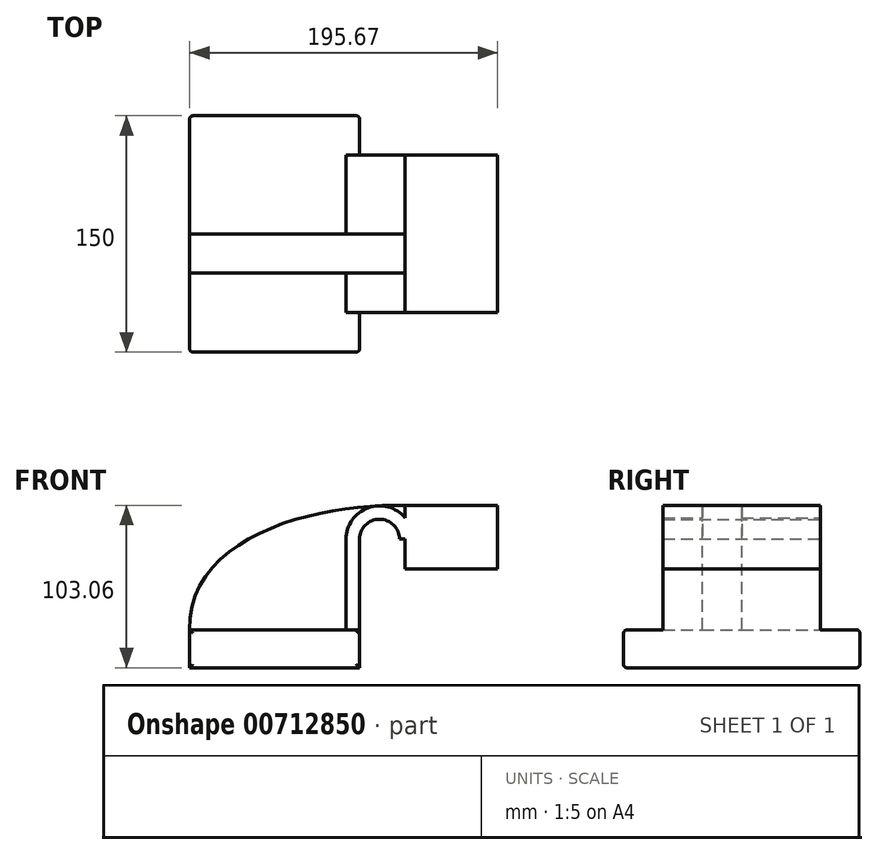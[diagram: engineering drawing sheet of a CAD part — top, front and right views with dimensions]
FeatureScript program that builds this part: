
annotation { "Feature Type Name" : "Feature", "Feature Type Description" : "" }
export const myFeature = defineFeature(function(context is Context, id is Id, definition is map)
    precondition{}
    {
        {
            var Q0;
            Q0=qCreatedBy(makeId("Front.planeOp"),FACE);
            var sketch = newSketch(context, id + "F0", { "sketchPlane" : qUnion([Q0])});
            skLineSegment(sketch, "E0.bottom", {"start": v(-53.96, 12) * mm, "end": v(53.96, 12) * mm});
            skLineSegment(sketch, "E0.top", {"start": v(-53.96, -12) * mm, "end": v(53.96, -12) * mm});
            skLineSegment(sketch, "E0.left", {"start": v(-53.96, 12) * mm, "end": v(-53.96, -12) * mm});
            skLineSegment(sketch, "E0.right", {"start": v(53.96, 12) * mm, "end": v(53.96, -12) * mm});
            skPoint(sketch, "E0.middle", {"position": v(0, 0) * mm});
            skLineSegment(sketch, "E1.bottom", {"start": v(82.9, 50.87) * mm, "end": v(141.7, 50.87) * mm});
            skLineSegment(sketch, "E1.top", {"start": v(82.9, 90.9) * mm, "end": v(141.7, 90.9) * mm});
            skLineSegment(sketch, "E1.left", {"start": v(82.9, 50.87) * mm, "end": v(82.9, 90.9) * mm});
            skLineSegment(sketch, "E1.right", {"start": v(141.7, 50.87) * mm, "end": v(141.7, 90.9) * mm});
            skPoint(sketch, "E1.middle", {"position": v(112.3, 70.89) * mm});
            skLineSegment(sketch, "E2", {"start": v(53.96, 12) * mm, "end": v(53.96, 69.64) * mm});
            skArc(sketch, "E3", {"start": v(53.96, 69.64) * mm, "mid": v(66.63, 82.31) * mm, "end": v(79.3, 69.64) * mm});
            skLineSegment(sketch, "E4", {"start": v(79.3, 69.64) * mm, "end": v(104.51, 69.64) * mm});
            skLineSegment(sketch, "E5.0", {"start": v(86.04, 78.16) * mm, "end": v(104.51, 78.16) * mm});
            skArc(sketch, "E5.1", {"start": v(45.43, 69.64) * mm, "mid": v(62.28, 90.38) * mm, "end": v(86.04, 78.16) * mm});
            skLineSegment(sketch, "E5.2", {"start": v(45.43, 12) * mm, "end": v(45.43, 69.64) * mm});
            skLineSegment(sketch, "E6", {"start": v(98.34, 78.16) * mm, "end": v(98.34, 69.64) * mm});
            skFitSpline(sketch, "E7", {"points": [v(-53.96, 12) * mm, v(82.9, 90.9) * mm], "startDerivative": vector(-4.4, 181.92) * mm, "endDerivative": vector(159.62, -6.55) * mm});
            skSolve(sketch);
        }
        {
            var Q0;
            Q0=makeQuery(id+"F0.imprint","IMPRINT",FACE,{"disambiguationData":[TD([[makeQuery(id+"F0.imprint","IMPRINT",EDGE,{"derivedFrom":sQuery(id+"F0.wireOp",EDGE,"E0.top")}),1.0]])]});
            var sketch = newSketch(context, id + "F1", { "sketchPlane" : qUnion([Q0])});
            skSolve(sketch);
        }
        {
            var Q0;
            {var subQ5=sQuery(id+"F0.wireOp",EDGE,"E6");Q0=makeQuery(id+"F0.imprint","IMPRINT",FACE,{"disambiguationData":[TD([[makeQuery(id+"F0.imprint","IMPRINT",EDGE,{"derivedFrom":subQ5}),-1.0]])]});}
            var Q1;
            {var subQ4=sQuery(id+"F0.wireOp",EDGE,"E1.bottom");Q1=makeQuery(id+"F0.imprint","IMPRINT",FACE,{"disambiguationData":[TD([[makeQuery(id+"F0.imprint","IMPRINT",EDGE,{"derivedFrom":subQ4}),1.0]])]});}
            var Q2;
            {var subQ1=sQuery(id+"F0.wireOp",EDGE,"E2");Q2=makeQuery(id+"F0.imprint","IMPRINT",FACE,{"disambiguationData":[TD([[makeQuery(id+"F0.imprint","IMPRINT",EDGE,{"derivedFrom":subQ1}),1.0]])]});}
            extrude(context, id + "F2", {"entities" : qUnion([Q0, Q1, Q2]), "endBound" : BoundingType.SYMMETRIC, "depth" : 100 * mm, "offsetDistance" : 25 * mm});
        }
        {
            var Q0;
            Q0=qSketchRegion(id+"F0",true);
            extrude(context, id + "F3", {"entities" : qUnion([Q0]), "operationType" : NewBodyOperationType.ADD, "depth" : 25 * mm, "offsetDistance" : 25 * mm});
        }
        {
            var Q0;
            Q0=makeQuery(id+"F0.imprint","IMPRINT",FACE,{"disambiguationData":[TD([[makeQuery(id+"F0.imprint","IMPRINT",EDGE,{"derivedFrom":sQuery(id+"F0.wireOp",EDGE,"E0.top")}),1.0]])]});
            extrude(context, id + "F4", {"entities" : qUnion([Q0]), "operationType" : NewBodyOperationType.ADD, "endBound" : BoundingType.SYMMETRIC, "depth" : 50 * mm, "offsetDistance" : 25 * mm});
        }
        {
            var Q0;
            Q0=makeQuery(id+"F2.opExtrude","CAP_EDGE",EDGE,{"disambiguationData":[OSD([sQuery(id+"F0.wireOp",EDGE,"E1.right")])],"isStart":true});
            var Q1;
            Q1=sQuery(id+"F0.wireOp",EDGE,"E1.right");
            revolve(context, id + "F5", {"bodyType" : ToolBodyType.SURFACE, "operationType" : NewBodyOperationType.ADD, "surfaceOperationType" : NewSurfaceOperationType.NEW, "surfaceEntities" : qUnion([Q0]), "axis" : qUnion([Q1]), "revolveType" : RevolveType.FULL});
        }
        {
            var Q0;
            Q0=makeQuery(id+"F1.imprint","IMPRINT",FACE,{"disambiguationData":[TD([[makeQuery(id+"F1.imprint","IMPRINT",EDGE,{"derivedFrom":makeQuery(id+"F0.imprint","IMPRINT",EDGE,{"derivedFrom":sQuery(id+"F0.wireOp",EDGE,"E0.top")})}),1.0]])]});
            extrude(context, id + "F6", {"entities" : qUnion([Q0]), "operationType" : NewBodyOperationType.ADD, "endBound" : BoundingType.SYMMETRIC, "depth" : 150 * mm, "offsetDistance" : 25 * mm});
        }
        {
            var Q0;
            Q0=makeQuery(id+"F6.opExtrude","CAP_FACE",FACE,{"disambiguationData":[OSD([sQuery(id+"F0.wireOp",EDGE,"E0.bottom"),sQuery(id+"F0.wireOp",EDGE,"E0.top"),sQuery(id+"F0.wireOp",EDGE,"E0.left"),sQuery(id+"F0.wireOp",EDGE,"E0.right")])],"isStart":false});
            var Q1;
            Q1=makeQuery(id+"F6.opExtrude","CAP_FACE",FACE,{"disambiguationData":[OSD([sQuery(id+"F0.wireOp",EDGE,"E0.bottom"),sQuery(id+"F0.wireOp",EDGE,"E0.top"),sQuery(id+"F0.wireOp",EDGE,"E0.left"),sQuery(id+"F0.wireOp",EDGE,"E0.right")])],"isStart":true});
            fillet(context, id + "F7", {"entities" : qUnion([Q0, Q1]), "radius" : 2 * mm, "tangentPropagation" : true, "allowEdgeOverflow" : false});
        }
    });
